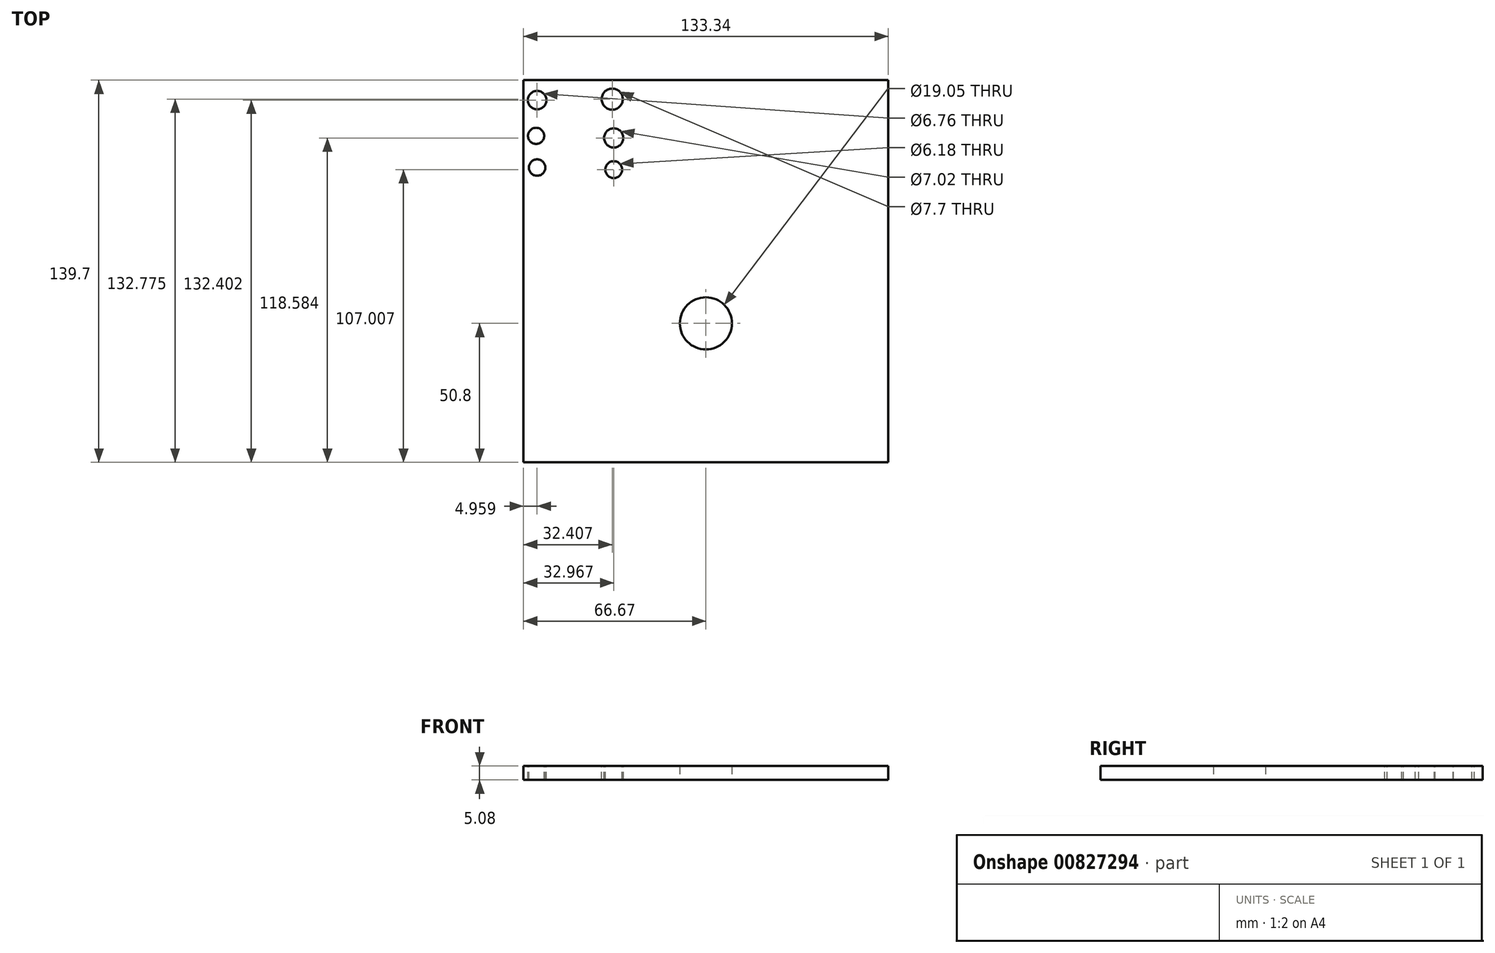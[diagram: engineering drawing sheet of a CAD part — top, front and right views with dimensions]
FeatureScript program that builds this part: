
annotation { "Feature Type Name" : "Feature", "Feature Type Description" : "" }
export const myFeature = defineFeature(function(context is Context, id is Id, definition is map)
    precondition{}
    {
        {
            var Q0;
            Q0=qCreatedBy(makeId("Top.planeOp"),FACE);
            var sketch = newSketch(context, id + "F0", { "sketchPlane" : qUnion([Q0])});
            skLineSegment(sketch, "E0.bottom", {"start": v(-66.67, -69.85) * mm, "end": v(66.68, -69.85) * mm});
            skLineSegment(sketch, "E0.top", {"start": v(-66.68, 69.85) * mm, "end": v(66.67, 69.85) * mm});
            skLineSegment(sketch, "E0.left", {"start": v(-66.67, -69.85) * mm, "end": v(-66.68, 69.85) * mm});
            skLineSegment(sketch, "E0.right", {"start": v(66.68, -69.85) * mm, "end": v(66.67, 69.85) * mm});
            skPoint(sketch, "E0.middle", {"position": v(0, 0) * mm});
            skSolve(sketch);
        }
        {
            var Q0;
            Q0=makeQuery(id+"F0.imprint","IMPRINT",FACE,{"disambiguationData":[TD([[makeQuery(id+"F0.imprint","IMPRINT",EDGE,{"derivedFrom":sQuery(id+"F0.wireOp",EDGE,"E0.bottom")}),1.0]])]});
            extrude(context, id + "F1", {"entities" : qUnion([Q0]), "depth" : 5.08 * mm, "offsetDistance" : 25.4 * mm});
        }
        {
            var Q0;
            Q0=qCreatedBy(makeId("Top.planeOp"),FACE);
            var sketch = newSketch(context, id + "F2", { "sketchPlane" : qUnion([Q0])});
            skPoint(sketch, "E1.0", {"position": v(0, -69.85) * mm});
            skCircle(sketch, "E2", {"center": v(0, -19.05) * mm, "radius": 9.53 * mm});
            skSolve(sketch);
        }
        {
            var Q0;
            Q0 = qSketchRegion(id + "F2", true);
            extrude(context, id + "F3", {"entities" : qUnion([Q0]), "operationType" : NewBodyOperationType.REMOVE, "depth" : 27.18 * mm, "offsetDistance" : 25.4 * mm});
        }
        {
            var Q0;
            Q0=makeQuery(id+"F1.opExtrude","CAP_FACE",FACE,{"disambiguationData":[OSD([sQuery(id+"F0.wireOp",EDGE,"E0.bottom"),sQuery(id+"F0.wireOp",EDGE,"E0.top"),sQuery(id+"F0.wireOp",EDGE,"E0.left"),sQuery(id+"F0.wireOp",EDGE,"E0.right")])],"isStart":false});
            var sketch = newSketch(context, id + "F4", { "sketchPlane" : qUnion([Q0])});
            skCircle(sketch, "E3", {"center": v(-61.71, 62.55) * mm, "radius": 3.38 * mm});
            skCircle(sketch, "E4", {"center": v(-61.71, 37.9) * mm, "radius": 3 * mm});
            skCircle(sketch, "E5", {"center": v(-62.08, 49.48) * mm, "radius": 2.95 * mm});
            skCircle(sketch, "E6", {"center": v(-34.26, 62.93) * mm, "radius": 3.85 * mm});
            skCircle(sketch, "E7", {"center": v(-33.7, 48.73) * mm, "radius": 3.5 * mm});
            skCircle(sketch, "E8", {"center": v(-33.7, 37.16) * mm, "radius": 3.1 * mm});
            skSolve(sketch);
        }
        {
            var Q0;
            Q0 = qSketchRegion(id + "F4", true);
            extrude(context, id + "F5", {"entities" : qUnion([Q0]), "operationType" : NewBodyOperationType.REMOVE, "oppositeDirection" : true, "depth" : 25.4 * mm, "offsetDistance" : 25.4 * mm});
        }
    });
